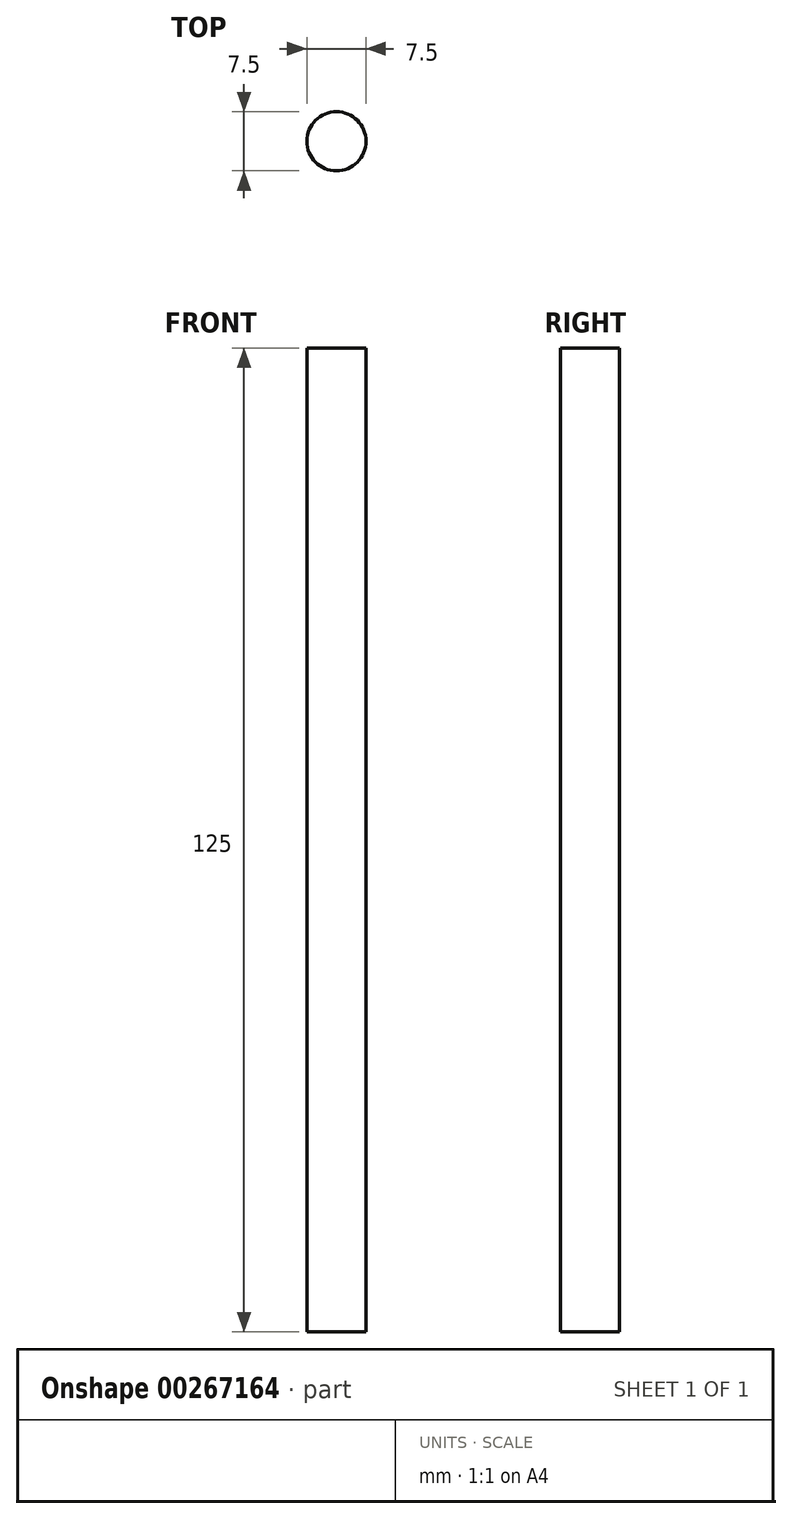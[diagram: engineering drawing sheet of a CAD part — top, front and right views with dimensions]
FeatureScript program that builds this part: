
annotation { "Feature Type Name" : "Feature", "Feature Type Description" : "" }
export const myFeature = defineFeature(function(context is Context, id is Id, definition is map)
    precondition{}
    {
        {
            var Q0;
            Q0=qCreatedBy(makeId("Top.planeOp"),FACE);
            var sketch = newSketch(context, id + "F0", { "sketchPlane" : qUnion([Q0])});
            skCircle(sketch, "E0", {"center": v(0, 0) * mm, "radius": 3.75 * mm});
            skSolve(sketch);
        }
        {
            var Q0;
            Q0=makeQuery(id+"F0.imprint","IMPRINT",FACE,{"disambiguationData":[TD([[makeQuery(id+"F0.imprint","IMPRINT",EDGE,{"derivedFrom":sQuery(id+"F0.wireOp",EDGE,"E0")}),1.0]])]});
            extrude(context, id + "F1", {"entities" : qUnion([Q0]), "oppositeDirection" : true, "depth" : 125 * mm});
        }
    });
